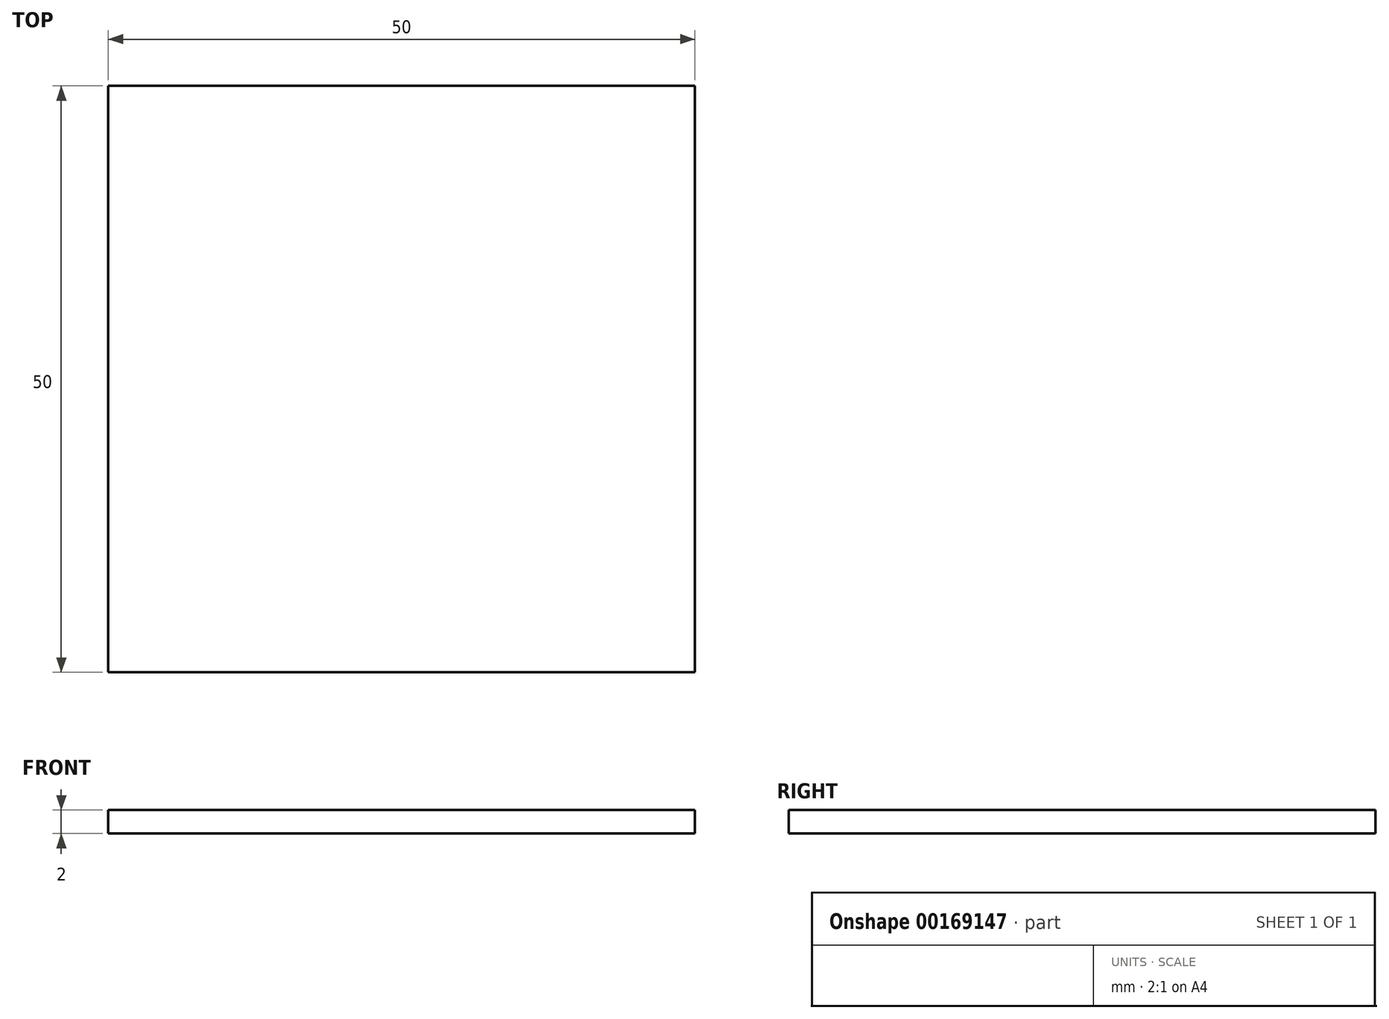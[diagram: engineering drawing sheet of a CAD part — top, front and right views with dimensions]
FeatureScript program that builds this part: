
annotation { "Feature Type Name" : "Feature", "Feature Type Description" : "" }
export const myFeature = defineFeature(function(context is Context, id is Id, definition is map)
    precondition{}
    {
        {
            var Q0;
            Q0=qCreatedBy(makeId("Top.planeOp"),FACE);
            var sketch = newSketch(context, id + "F0", { "sketchPlane" : qUnion([Q0])});
            skLineSegment(sketch, "E0.bottom", {"start": v(25, 25) * mm, "end": v(-25, 25) * mm});
            skLineSegment(sketch, "E0.top", {"start": v(25, -25) * mm, "end": v(-25, -25) * mm});
            skLineSegment(sketch, "E0.left", {"start": v(25, 25) * mm, "end": v(25, -25) * mm});
            skLineSegment(sketch, "E0.right", {"start": v(-25, 25) * mm, "end": v(-25, -25) * mm});
            skPoint(sketch, "E0.middle", {"position": v(0, 0) * mm});
            skSolve(sketch);
        }
        {
            var Q0;
            Q0 = qSketchRegion(id + "F0", true);
            extrude(context, id + "F1", {"entities" : qUnion([Q0]), "depth" : 2 * mm});
        }
    });
